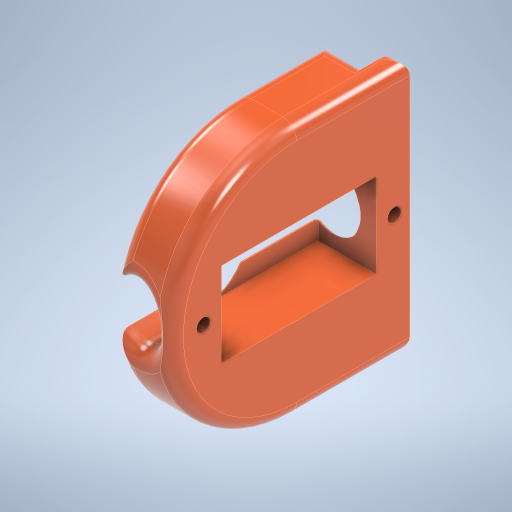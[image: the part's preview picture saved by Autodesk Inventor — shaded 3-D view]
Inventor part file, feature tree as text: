
AUTODESK INVENTOR PART (.ipt)
format: ipt  version: 2023.2 (Build 272271000, 271)  size: 458,752 bytes
history: native  units: mm
features: sketch x9, extrude x6, hole x3, fillet x2
ambient origin geometry x8: Origin, YZ Plane, XZ Plane, XY Plane, X Axis, Y Axis, Z Axis, Center Point
bodies: Solid1 (feature_tree)
feature tree (20):
  extrude  "Extrusion1"  Depth=12.6mm
  extrude  "Extrusion2"  Depth=8.0mm
  hole  "Hole1"  [1 undecoded]
  hole  "Hole2"  [1 undecoded]
  fillet  "Fillet1"  Radius=27.8mm
  hole  "Hole3"  [1 undecoded]
  extrude  "Extrusion3"  Depth=8.5mm TaperAngle=0.0deg
  extrude  "Extrusion4"  Depth=10.0mm TaperAngle=0.0deg
  extrude  "Extrusion5"  Depth=2.0mm TaperAngle=0.0deg
  extrude  "Extrusion6"  Depth=2.0mm
  fillet  "Fillet2"  [1 undecoded]
  sketch  "Sketch3"  dims[d0=37.0mm d1=12.6mm]
  sketch  "Sketch4"  dims[d2=35.0mm d3=0.0mm d4=8.0mm]
  sketch  "Sketch5"  dims[d5=3.8mm d6=0.0mm d7=24.1mm]
  sketch  "Sketch6"  dims[d8=2.0mm d9=6.0mm d10=4.0mm d11=2.0mm d12=90.0deg d13=8.0mm d14=0.0mm]
  sketch  "Sketch8"  dims[d15=8.0mm d16=6.0mm d17=4.0mm d18=2.0mm d19=90.0deg d20=8.0mm d21=0.0mm d22=2.0mm d25=27.8mm]
  sketch  "Sketch9"  dims[d26=4.502mm]
  sketch  "Sketch10"  dims[d27=2.0mm d28=6.0mm d29=4.0mm d30=2.0mm d31=90.0deg d32=8.0mm d33=0.0mm d34=12.4mm]
  sketch  "Sketch11"  dims[d35=22.6mm d36=8.5mm d37=0.0mm]
  sketch  "Sketch12"  dims[d38=6.1mm d39=10.0mm d40=0.0mm d41=35.0mm d42=0.0mm d43=4.0mm d44=0.0mm d45=0.0mm d46=2.0mm d47=0.0mm d48=0.0mm d49=0.0mm]
note: 4 required parameter values undecoded (feature->parameter linkage not recoverable at this tier; creation-order binding heuristic only, values carry confidence <= 0.55)
